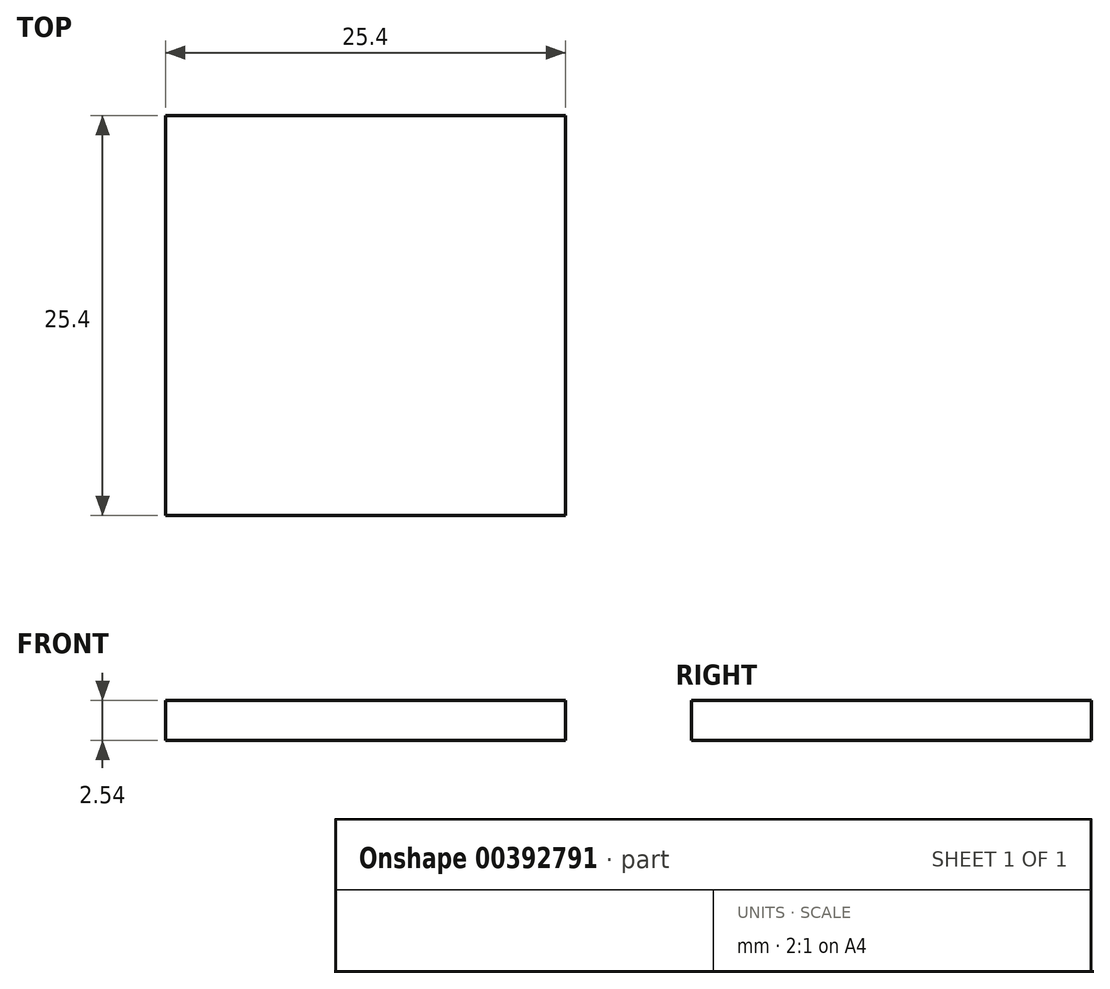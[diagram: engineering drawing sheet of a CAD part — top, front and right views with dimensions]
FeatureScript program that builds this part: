
annotation { "Feature Type Name" : "Feature", "Feature Type Description" : "" }
export const myFeature = defineFeature(function(context is Context, id is Id, definition is map)
    precondition{}
    {
        {
            var Q0;
            Q0=qCreatedBy(makeId("Top.planeOp"),FACE);
            var sketch = newSketch(context, id + "F0", { "sketchPlane" : qUnion([Q0])});
            skLineSegment(sketch, "E0.bottom", {"start": v(12.7, -12.7) * mm, "end": v(-12.7, -12.7) * mm});
            skLineSegment(sketch, "E0.top", {"start": v(12.7, 12.7) * mm, "end": v(-12.7, 12.7) * mm});
            skLineSegment(sketch, "E0.left", {"start": v(12.7, -12.7) * mm, "end": v(12.7, 12.7) * mm});
            skLineSegment(sketch, "E0.right", {"start": v(-12.7, -12.7) * mm, "end": v(-12.7, 12.7) * mm});
            skPoint(sketch, "E0.middle", {"position": v(0, 0) * mm});
            skSolve(sketch);
        }
        {
            var Q0;
            Q0 = qSketchRegion(id + "F0", true);
            extrude(context, id + "F1", {"entities" : qUnion([Q0]), "depth" : 2.54 * mm});
        }
    });
